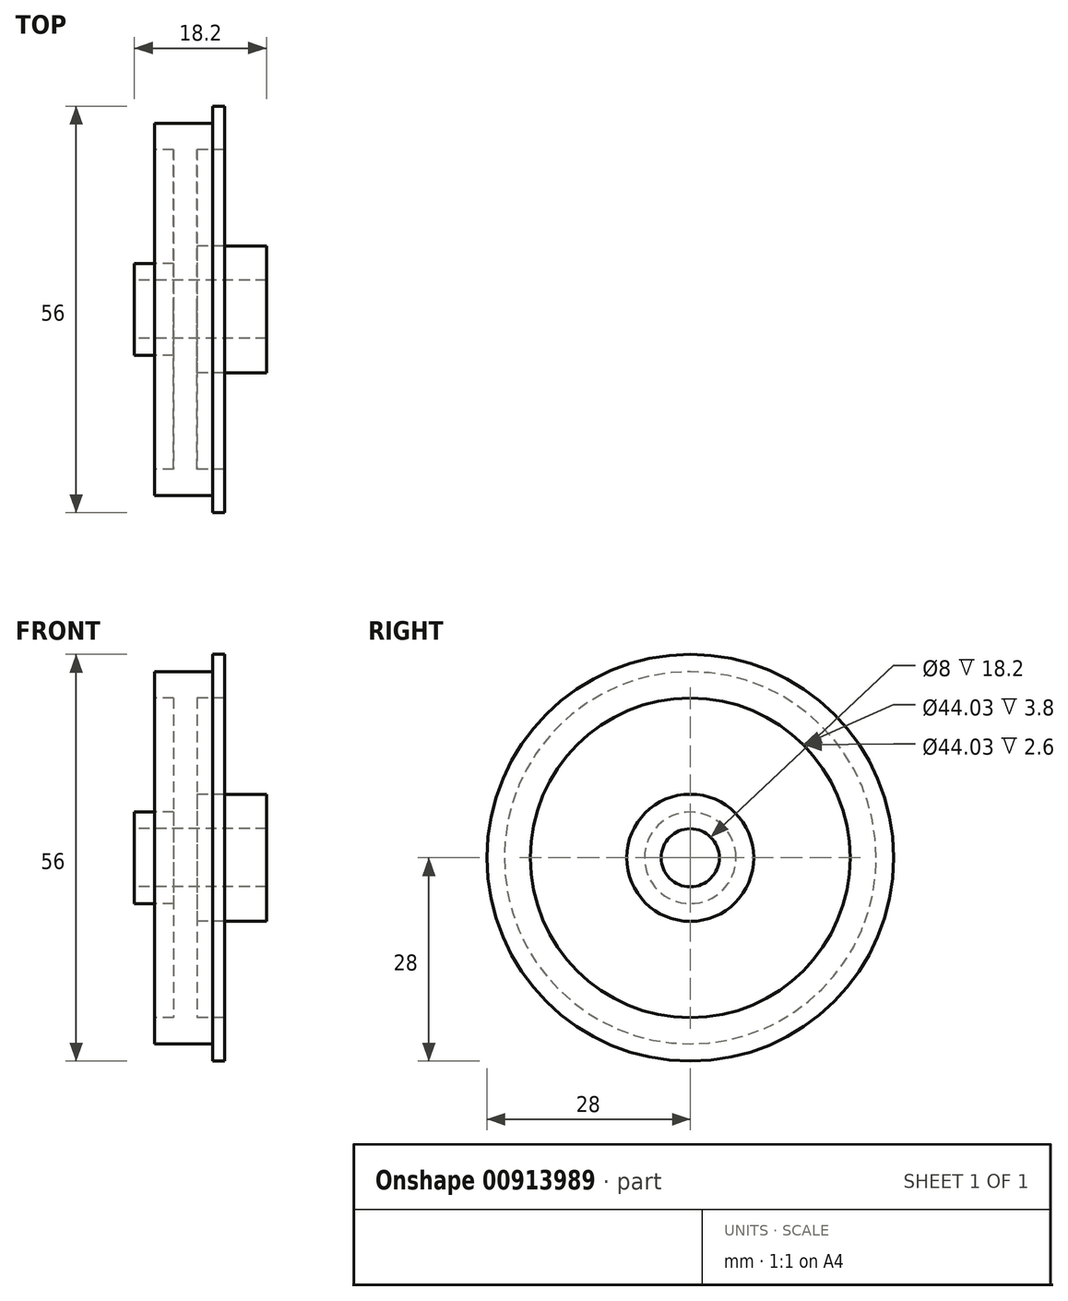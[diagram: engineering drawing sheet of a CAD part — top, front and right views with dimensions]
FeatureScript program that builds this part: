
annotation { "Feature Type Name" : "Feature", "Feature Type Description" : "" }
export const myFeature = defineFeature(function(context is Context, id is Id, definition is map)
    precondition{}
    {
        {
            var Q0;
            Q0=qCreatedBy(makeId("Front.planeOp"),FACE);
            var sketch = newSketch(context, id + "F0", { "sketchPlane" : qUnion([Q0])});
            skLineSegment(sketch, "E0", {"start": v(0, 0) * mm, "end": v(18.2, 0) * mm, "construction": true});
            skLineSegment(sketch, "E1", {"start": v(0, 4) * mm, "end": v(18.2, 4) * mm});
            skLineSegment(sketch, "E2", {"start": v(18.2, 4) * mm, "end": v(18.2, 8.75) * mm});
            skLineSegment(sketch, "E3", {"start": v(18.2, 8.75) * mm, "end": v(8.65, 8.75) * mm});
            skLineSegment(sketch, "E4", {"start": v(8.65, 8.75) * mm, "end": v(8.65, 22.01) * mm});
            skLineSegment(sketch, "E5", {"start": v(8.65, 22.01) * mm, "end": v(12.45, 22.01) * mm});
            skLineSegment(sketch, "E6", {"start": v(12.45, 22.01) * mm, "end": v(12.45, 28) * mm});
            skLineSegment(sketch, "E7", {"start": v(12.45, 28) * mm, "end": v(10.8, 28) * mm});
            skLineSegment(sketch, "E8", {"start": v(10.8, 28) * mm, "end": v(10.8, 25.61) * mm});
            skLineSegment(sketch, "E9", {"start": v(10.8, 25.61) * mm, "end": v(2.8, 25.61) * mm});
            skLineSegment(sketch, "E10", {"start": v(5.4, 22.01) * mm, "end": v(5.4, 6.3) * mm});
            skLineSegment(sketch, "E11", {"start": v(0, 6.3) * mm, "end": v(0, 4) * mm});
            skLineSegment(sketch, "E12", {"start": v(2.8, 25.61) * mm, "end": v(2.8, 22.01) * mm});
            skLineSegment(sketch, "E13", {"start": v(2.8, 22.01) * mm, "end": v(5.4, 22.01) * mm});
            skLineSegment(sketch, "E14", {"start": v(0, 6.3) * mm, "end": v(5.4, 6.3) * mm});
            skSolve(sketch);
        }
        {
            var Q0;
            Q0=makeQuery(id+"F0.imprint","IMPRINT",FACE,{"disambiguationData":[TD([[makeQuery(id+"F0.imprint","IMPRINT",EDGE,{"derivedFrom":sQuery(id+"F0.wireOp",EDGE,"E1")}),1.0]])]});
            var Q1;
            Q1=sQuery(id+"F0.wireOp",EDGE,"E0");
            revolve(context, id + "F1", {"surfaceOperationType" : NewSurfaceOperationType.NEW, "entities" : qUnion([Q0]), "axis" : qUnion([Q1]), "revolveType" : RevolveType.FULL});
        }
    });
